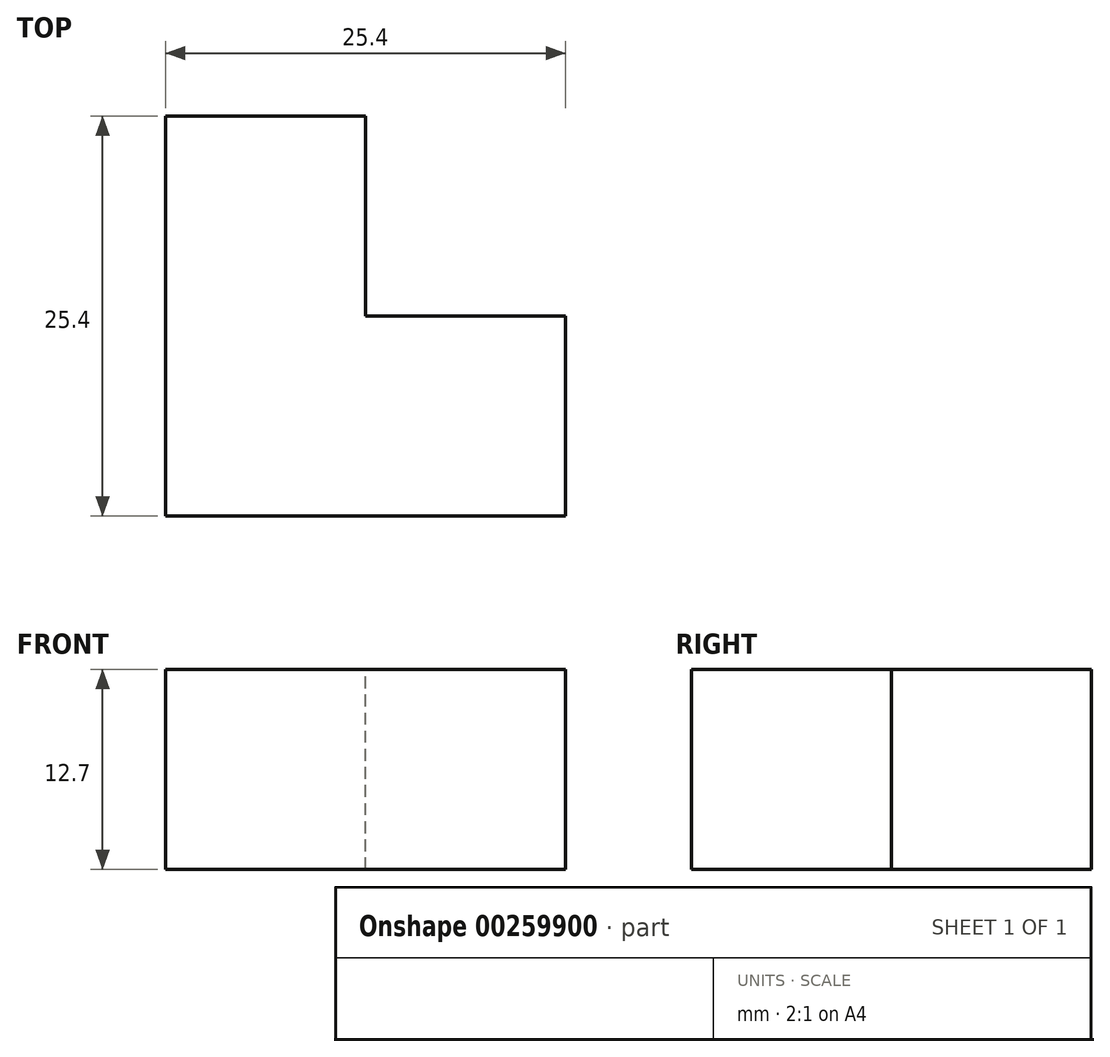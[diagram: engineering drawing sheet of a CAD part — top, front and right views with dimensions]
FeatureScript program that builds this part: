
annotation { "Feature Type Name" : "Feature", "Feature Type Description" : "" }
export const myFeature = defineFeature(function(context is Context, id is Id, definition is map)
    precondition{}
    {
        {
            var Q0;
            Q0=qCreatedBy(makeId("Right.planeOp"),FACE);
            var sketch = newSketch(context, id + "F0", { "sketchPlane" : qUnion([Q0])});
            skLineSegment(sketch, "E0", {"start": v(0, 0) * mm, "end": v(0, 37.95) * mm});
            skLineSegment(sketch, "E1", {"start": v(0, 37.95) * mm, "end": v(25.4, 37.95) * mm});
            skLineSegment(sketch, "E2", {"start": v(25.4, 37.95) * mm, "end": v(25.4, 25.25) * mm});
            skLineSegment(sketch, "E3", {"start": v(25.4, 25.25) * mm, "end": v(12.7, 25.25) * mm});
            skLineSegment(sketch, "E4", {"start": v(12.7, 25.25) * mm, "end": v(12.7, 12.55) * mm});
            skLineSegment(sketch, "E5", {"start": v(12.7, 12.55) * mm, "end": v(25.4, 12.55) * mm});
            skLineSegment(sketch, "E6", {"start": v(25.4, 12.7) * mm, "end": v(25.4, 0) * mm});
            skLineSegment(sketch, "E7", {"start": v(25.4, 0) * mm, "end": v(0, 0) * mm});
            skLineSegment(sketch, "E8.bottom", {"start": v(12.7, 25.25) * mm, "end": v(0, 25.25) * mm});
            skLineSegment(sketch, "E8.top", {"start": v(12.7, 37.95) * mm, "end": v(0, 37.95) * mm});
            skLineSegment(sketch, "E8.left", {"start": v(12.7, 25.25) * mm, "end": v(12.7, 37.95) * mm});
            skLineSegment(sketch, "E8.right", {"start": v(0, 25.25) * mm, "end": v(0, 37.95) * mm});
            skSolve(sketch);
        }
        {
            var Q0;
            Q0=makeQuery(id+"F0.imprint","IMPRINT",FACE,{"disambiguationData":[TD([[makeQuery(id+"F0.imprint","IMPRINT",EDGE,{"derivedFrom":sQuery(id+"F0.wireOp",EDGE,"E8.bottom")}),-1.0]])]});
            extrude(context, id + "F1", {"entities" : qUnion([Q0]), "depth" : 25.4 * mm});
        }
        {
            var Q0;
            Q0=makeQuery(id+"F0.imprint","IMPRINT",FACE,{"disambiguationData":[TD([[makeQuery(id+"F0.imprint","IMPRINT",EDGE,{"derivedFrom":sQuery(id+"F0.wireOp",EDGE,"E0")}),-1.0]])]});
            var Q1;
            Q1=makeQuery(id+"F0.imprint","IMPRINT",FACE,{"disambiguationData":[TD([[makeQuery(id+"F0.imprint","IMPRINT",EDGE,{"derivedFrom":sQuery(id+"F0.wireOp",EDGE,"E1")}),-1.0]])]});
            extrude(context, id + "F2", {"entities" : qUnion([Q0, Q1]), "operationType" : NewBodyOperationType.ADD, "depth" : 12.7 * mm});
        }
    });
